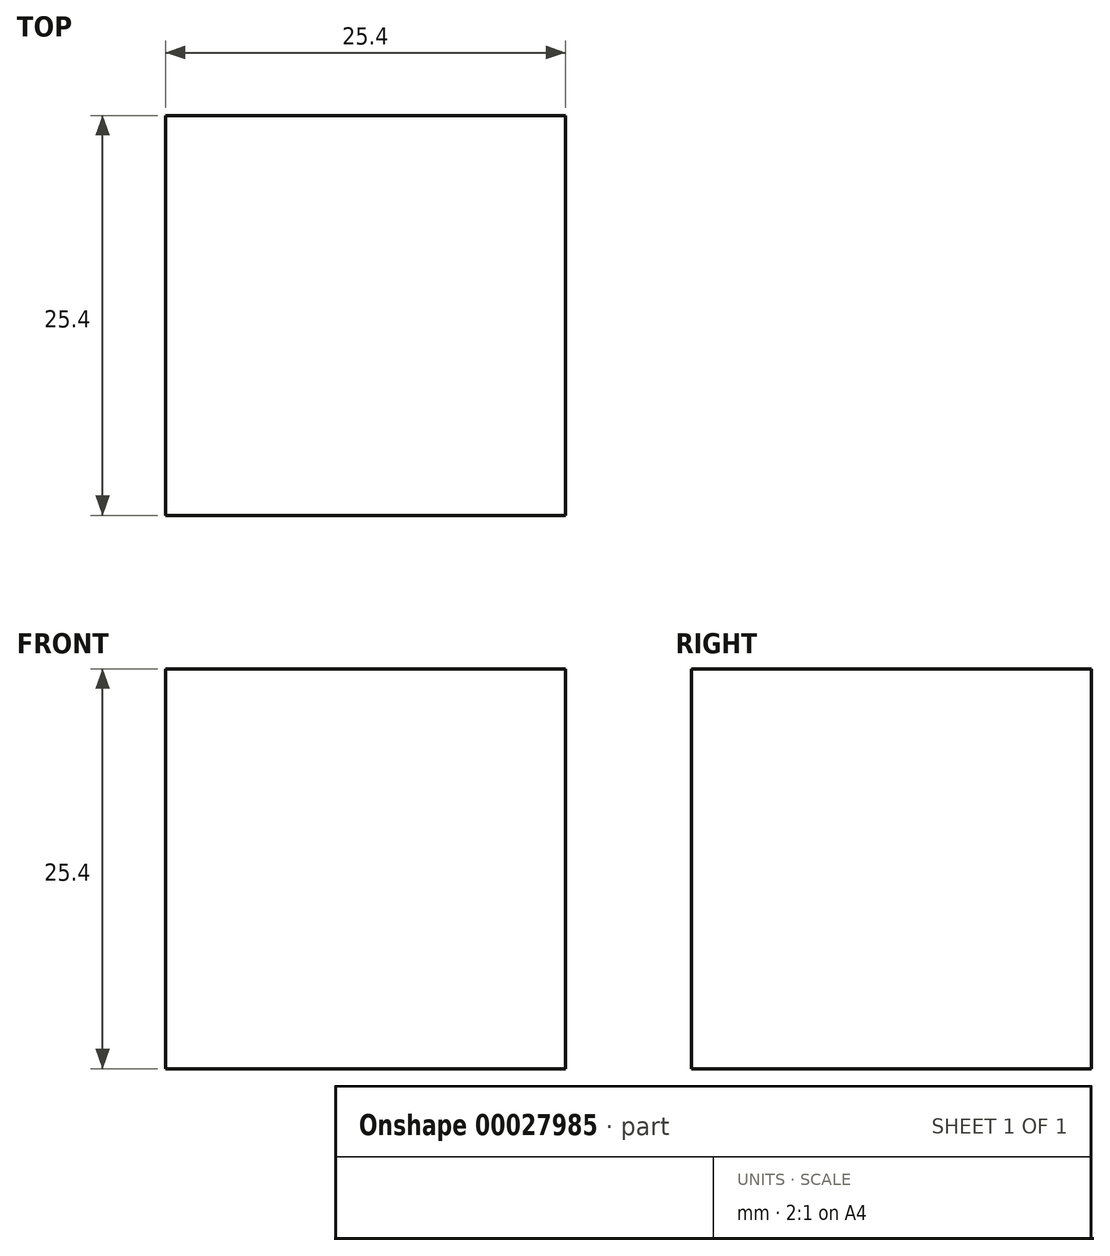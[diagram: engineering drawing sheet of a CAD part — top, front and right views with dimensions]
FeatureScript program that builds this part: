
annotation { "Feature Type Name" : "Feature", "Feature Type Description" : "" }
export const myFeature = defineFeature(function(context is Context, id is Id, definition is map)
    precondition{}
    {
        {
            var Q0;
            Q0=qCreatedBy(makeId("Top.planeOp"),FACE);
            var sketch = newSketch(context, id + "F0", { "sketchPlane" : qUnion([Q0])});
            skLineSegment(sketch, "E0.rect.bottom", {"start": v(-12.7, 12.7) * mm, "end": v(12.7, 12.7) * mm});
            skLineSegment(sketch, "E0.rect.top", {"start": v(-12.7, -12.7) * mm, "end": v(12.7, -12.7) * mm});
            skLineSegment(sketch, "E0.rect.left", {"start": v(-12.7, 12.7) * mm, "end": v(-12.7, -12.7) * mm});
            skLineSegment(sketch, "E0.rect.right", {"start": v(12.7, 12.7) * mm, "end": v(12.7, -12.7) * mm});
            skPoint(sketch, "E0.rect.middle", {"position": v(0, 0) * mm});
            skSolve(sketch);
        }
        {
            var Q0;
            Q0=makeQuery(id+"F0.imprint","IMPRINT",FACE,{"disambiguationData":[TD([[makeQuery(id+"F0.imprint","IMPRINT",EDGE,{"derivedFrom":sQuery(id+"F0.wireOp",EDGE,"E0.rect.bottom")}),-1.0]])]});
            extrude(context, id + "F1", {"entities" : qUnion([Q0]), "depth" : 25.4 * mm});
        }
    });
